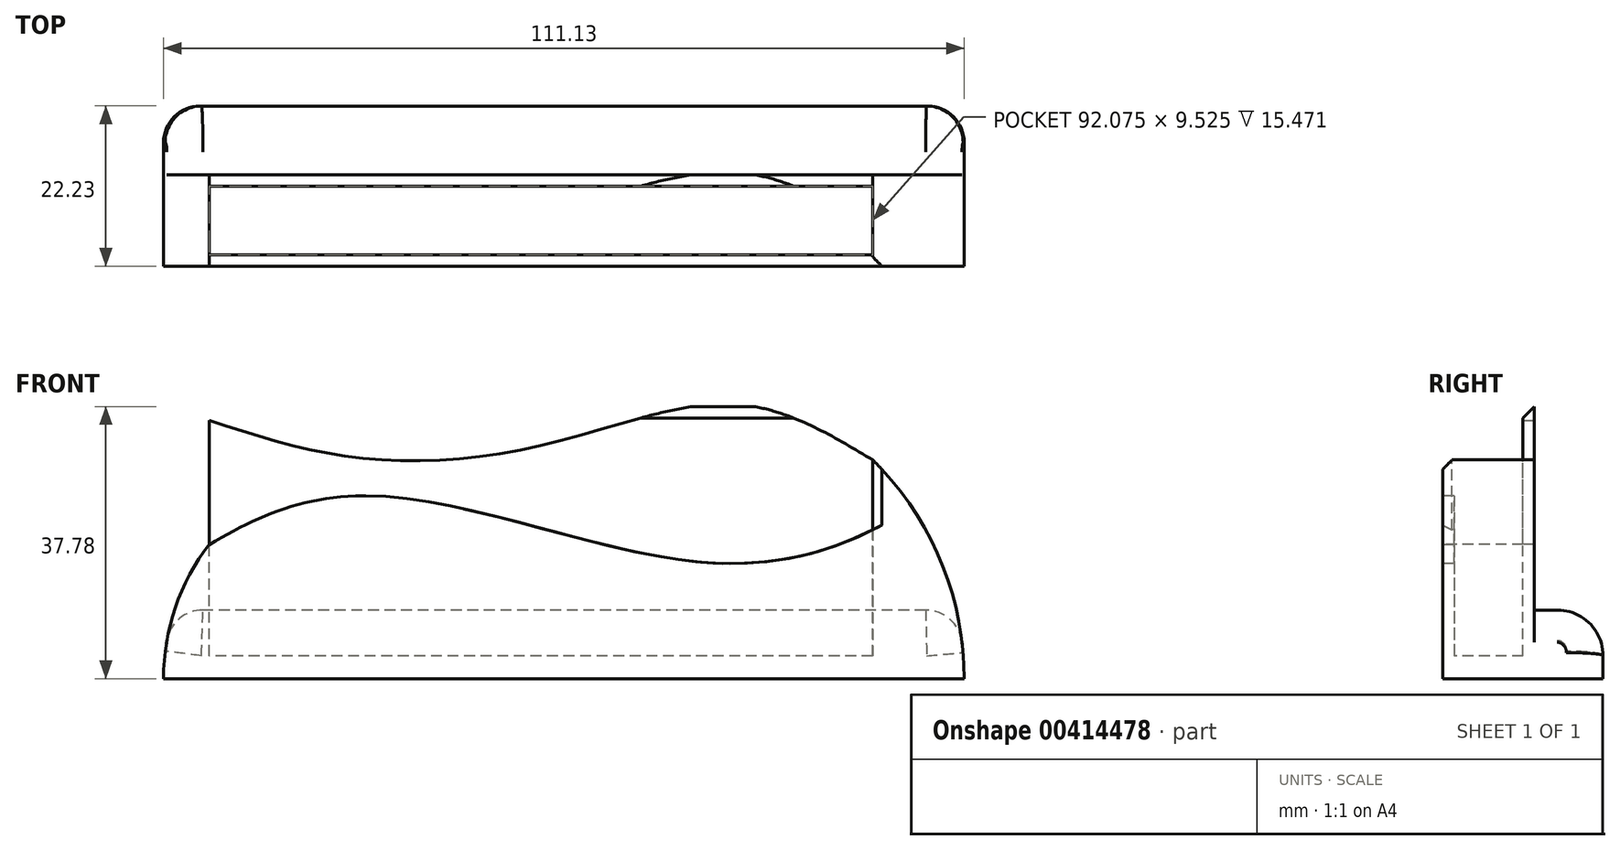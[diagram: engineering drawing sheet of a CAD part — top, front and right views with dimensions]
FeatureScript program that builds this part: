
annotation { "Feature Type Name" : "Feature", "Feature Type Description" : "" }
export const myFeature = defineFeature(function(context is Context, id is Id, definition is map)
    precondition{}
    {
        {
            var Q0;
            Q0=qCreatedBy(makeId("Right.planeOp"),FACE);
            var sketch = newSketch(context, id + "F0", { "sketchPlane" : qUnion([Q0])});
            skLineSegment(sketch, "E0", {"start": v(0, 0) * mm, "end": v(0, 25.4) * mm});
            skLineSegment(sketch, "E1", {"start": v(0, 25.4) * mm, "end": v(1.59, 25.4) * mm});
            skLineSegment(sketch, "E2", {"start": v(1.59, 25.4) * mm, "end": v(1.59, 3.18) * mm});
            skLineSegment(sketch, "E3", {"start": v(1.59, 3.18) * mm, "end": v(11.11, 3.18) * mm});
            skLineSegment(sketch, "E4", {"start": v(11.11, 3.18) * mm, "end": v(11.11, 38.1) * mm});
            skLineSegment(sketch, "E5", {"start": v(11.11, 38.1) * mm, "end": v(12.7, 38.1) * mm});
            skLineSegment(sketch, "E6", {"start": v(12.7, 38.1) * mm, "end": v(12.7, 0) * mm});
            skLineSegment(sketch, "E7", {"start": v(12.7, 0) * mm, "end": v(0, 0) * mm});
            skSolve(sketch);
        }
        {
            var Q0;
            Q0=makeQuery(id+"F0.imprint","IMPRINT",FACE,{"disambiguationData":[TD([[makeQuery(id+"F0.imprint","IMPRINT",EDGE,{"derivedFrom":sQuery(id+"F0.wireOp",EDGE,"E0")}),-1.0]])]});
            extrude(context, id + "F1", {"entities" : qUnion([Q0]), "depth" : 92.07 * mm});
        }
        {
            var Q0;
            Q0=makeQuery(id+"F1.opExtrude","SWEPT_FACE",FACE,{"disambiguationData":[OSD([sQuery(id+"F0.wireOp",EDGE,"E0")])]});
            var sketch = newSketch(context, id + "F2", { "sketchPlane" : qUnion([Q0])});
            skFitSpline(sketch, "E8", {"points": [v(0, 18.6) * mm, v(21.38, 25.4) * mm, v(56.78, 18.13) * mm, v(92.08, 20.65) * mm], "startDerivative": vector(67.88, 41.03) * mm, "endDerivative": vector(105.85, 52.89) * mm});
            skSolve(sketch);
        }
        {
            var Q0;
            {var subQ0=sQuery(id+"F0.wireOp",EDGE,"E0");var subQ1=makeQuery(id+"F1.opExtrude","CAP_EDGE",EDGE,{"disambiguationData":[OSD([subQ0])],"isStart":true});var subQ2=sQuery(id+"F2.wireOp",EDGE,"E8");var subQ3=makeQuery(id+"F2.imprint","INTERSECT",VERTEX,{"derivedFrom":[subQ1,subQ2]});Q0=makeQuery(id+"F2.imprint","IMPRINT",FACE,{"disambiguationData":[TD([[makeQuery(id+"F2.imprint","IMPRINT",EDGE,{"disambiguationData":[TD([[subQ3,-1.0]])],"derivedFrom":subQ2}),1.0]])]});}
            var Q1;
            {var subQ0=sQuery(id+"F0.wireOp",EDGE,"E0");var subQ1=makeQuery(id+"F1.opExtrude","CAP_EDGE",EDGE,{"disambiguationData":[OSD([subQ0])],"isStart":false});var subQ2=sQuery(id+"F2.wireOp",EDGE,"E8");var subQ3=makeQuery(id+"F2.imprint","INTERSECT",VERTEX,{"derivedFrom":[subQ1,subQ2]});Q1=makeQuery(id+"F2.imprint","IMPRINT",FACE,{"disambiguationData":[TD([[makeQuery(id+"F2.imprint","IMPRINT",EDGE,{"disambiguationData":[TD([[subQ3,1.0]])],"derivedFrom":subQ2}),1.0]])]});}
            extrude(context, id + "F3", {"entities" : qUnion([Q0, Q1]), "operationType" : NewBodyOperationType.REMOVE, "endBound" : BoundingType.UP_TO_NEXT, "oppositeDirection" : true, "depth" : 25.4 * mm, "offsetDistance" : 25.4 * mm});
        }
        {
            var Q0;
            Q0=makeQuery(id+"F1.opExtrude","SWEPT_FACE",FACE,{"disambiguationData":[OSD([sQuery(id+"F0.wireOp",EDGE,"E6")])]});
            var sketch = newSketch(context, id + "F4", { "sketchPlane" : qUnion([Q0])});
            skFitSpline(sketch, "E9", {"points": [v(-92.08, 30.36) * mm, v(-72.87, 38.1) * mm, v(-46.83, 32.53) * mm, v(-20.34, 30.7) * mm, v(0, 35.84) * mm], "startDerivative": vector(78.4, 47.13) * mm, "endDerivative": vector(83.06, 27.16) * mm});
            skSolve(sketch);
        }
        {
            var Q0;
            {var subQ0=sQuery(id+"F0.wireOp",EDGE,"E6");var subQ1=makeQuery(id+"F1.opExtrude","CAP_EDGE",EDGE,{"disambiguationData":[OSD([subQ0])],"isStart":false});var subQ2=sQuery(id+"F4.wireOp",EDGE,"E9");var subQ3=makeQuery(id+"F4.imprint","INTERSECT",VERTEX,{"derivedFrom":[subQ1,subQ2]});Q0=makeQuery(id+"F4.imprint","IMPRINT",FACE,{"disambiguationData":[TD([[makeQuery(id+"F4.imprint","IMPRINT",EDGE,{"disambiguationData":[TD([[subQ3,-1.0]])],"derivedFrom":subQ2}),1.0]])]});}
            var Q1;
            {var subQ0=sQuery(id+"F0.wireOp",EDGE,"E6");var subQ1=makeQuery(id+"F1.opExtrude","CAP_EDGE",EDGE,{"disambiguationData":[OSD([subQ0])],"isStart":true});var subQ2=sQuery(id+"F4.wireOp",EDGE,"E9");var subQ3=makeQuery(id+"F4.imprint","INTERSECT",VERTEX,{"derivedFrom":[subQ1,subQ2]});Q1=makeQuery(id+"F4.imprint","IMPRINT",FACE,{"disambiguationData":[TD([[makeQuery(id+"F4.imprint","IMPRINT",EDGE,{"disambiguationData":[TD([[subQ3,1.0]])],"derivedFrom":subQ2}),1.0]])]});}
            extrude(context, id + "F5", {"entities" : qUnion([Q0, Q1]), "operationType" : NewBodyOperationType.REMOVE, "endBound" : BoundingType.UP_TO_NEXT, "oppositeDirection" : true, "depth" : 25.4 * mm, "offsetDistance" : 25.4 * mm});
        }
        {
            var Q0;
            Q0=makeQuery(id+"F1.opExtrude","SWEPT_FACE",FACE,{"disambiguationData":[OSD([sQuery(id+"F0.wireOp",EDGE,"E0")])]});
            var sketch = newSketch(context, id + "F6", { "sketchPlane" : qUnion([Q0])});
            skText(sketch, "E10", { "text": "FELONY", "fontName": "Tinos-Bold.ttf"});
            skLineSegment(sketch, "E11", {"start": v(46.04, 0) * mm, "end": v(46.04, 18.7) * mm, "construction": true});
            const initialGuessF6  = {"E10": [0.00287, 0.00127, 1, 0, 0.01499]};
            skSetInitialGuess(sketch, initialGuessF6);
            skSolve(sketch);
        }
        {
            var Q0;
            Q0=makeQuery(id+"F1.opExtrude","CAP_FACE",FACE,{"disambiguationData":[OSD([sQuery(id+"F0.wireOp",EDGE,"E0"),sQuery(id+"F0.wireOp",EDGE,"E1"),sQuery(id+"F0.wireOp",EDGE,"E2"),sQuery(id+"F0.wireOp",EDGE,"E3"),sQuery(id+"F0.wireOp",EDGE,"E4"),sQuery(id+"F0.wireOp",EDGE,"E5"),sQuery(id+"F0.wireOp",EDGE,"E6"),sQuery(id+"F0.wireOp",EDGE,"E7")])],"isStart":true});
            var sketch = newSketch(context, id + "F7", { "sketchPlane" : qUnion([Q0])});
            skLineSegment(sketch, "E12", {"start": v(-12.7, 3.18) * mm, "end": v(0, 3.17) * mm});
            skSolve(sketch);
        }
        {
            var Q0;
            {var subQ3=makeQuery(id+"F1.opExtrude","CAP_EDGE",EDGE,{"disambiguationData":[OSD([sQuery(id+"F0.wireOp",EDGE,"E7")])],"isStart":true});Q0=makeQuery(id+"F7.imprint","IMPRINT",FACE,{"disambiguationData":[TD([[makeQuery(id+"F7.imprint","IMPRINT",EDGE,{"derivedFrom":subQ3}),1.0]])]});}
            extrude(context, id + "F8", {"entities" : qUnion([Q0]), "operationType" : NewBodyOperationType.ADD, "depth" : 6.35 * mm});
        }
        {
            var Q0;
            Q0=makeQuery(id+"F8.boolean.opBoolean","MERGE",FACE,{"derivedFrom":[makeQuery(id+"F1.opExtrude","SWEPT_FACE",FACE,{"disambiguationData":[OSD([sQuery(id+"F0.wireOp",EDGE,"E3")])]}),makeQuery(id+"F8.opExtrude","SWEPT_FACE",FACE,{"disambiguationData":[OSD([sQuery(id+"F7.wireOp",EDGE,"E12")])]})]});
            var sketch = newSketch(context, id + "F9", { "sketchPlane" : qUnion([Q0])});
            skLineSegment(sketch, "E13", {"start": v(0, 11.11) * mm, "end": v(0, 1.59) * mm});
            skSolve(sketch);
        }
        {
            var Q0;
            Q0=makeQuery(id+"F9.imprint","IMPRINT",FACE,{"disambiguationData":[TD([[makeQuery(id+"F9.imprint","IMPRINT",EDGE,{"derivedFrom":sQuery(id+"F9.wireOp",EDGE,"E13")}),-1.0]])]});
            extrude(context, id + "F10", {"entities" : qUnion([Q0]), "operationType" : NewBodyOperationType.ADD, "depth" : 15.47 * mm});
        }
        {
            var Q0;
            {var subQ0=sQuery(id+"F0.wireOp",EDGE,"E0");var subQ1=sQuery(id+"F0.wireOp",EDGE,"E1");Q0=makeQuery(id+"F10.boolean.opBoolean","MERGE",FACE,{"derivedFrom":[makeQuery(id+"F8.boolean.opBoolean","MERGE",FACE,{"derivedFrom":[makeQuery(id+"FmbjE0y4cJYNi4l_1.boolean.opBoolean","SPLIT",FACE,{"disambiguationData":[TD([makeQuery(id+"F1.opExtrude","SWEPT_FACE",FACE,{"disambiguationData":[OSD([subQ1])]})])],"derivedFrom":makeQuery(id+"F1.opExtrude","SWEPT_FACE",FACE,{"disambiguationData":[OSD([subQ0])]})}),makeQuery(id+"F8.opExtrude","SWEPT_FACE",FACE,{"disambiguationData":[OSD([subQ0])]})]}),makeQuery(id+"F10.opExtrude","SWEPT_FACE",FACE,{"disambiguationData":[OSD([subQ0,sQuery(id+"F7.wireOp",EDGE,"E12")])]})]});}
            var sketch = newSketch(context, id + "F11", { "sketchPlane" : qUnion([Q0])});
            skArc(sketch, "E14", {"start": v(0, 18.65) * mm, "mid": v(-4.72, 9.85) * mm, "end": v(-6.35, 0) * mm});
            skSolve(sketch);
        }
        {
            var Q0;
            Q0=makeQuery(id+"F11.imprint","IMPRINT",FACE,{"disambiguationData":[TD([[makeQuery(id+"F11.imprint","IMPRINT",EDGE,{"derivedFrom":sQuery(id+"F11.wireOp",EDGE,"E14")}),-1.0]])]});
            extrude(context, id + "F12", {"entities" : qUnion([Q0]), "operationType" : NewBodyOperationType.REMOVE, "endBound" : BoundingType.UP_TO_NEXT, "oppositeDirection" : true, "depth" : 25.4 * mm});
        }
        {
            var Q0;
            Q0=makeQuery(id+"F1.opExtrude","CAP_FACE",FACE,{"disambiguationData":[OSD([sQuery(id+"F0.wireOp",EDGE,"E0"),sQuery(id+"F0.wireOp",EDGE,"E1"),sQuery(id+"F0.wireOp",EDGE,"E2"),sQuery(id+"F0.wireOp",EDGE,"E3"),sQuery(id+"F0.wireOp",EDGE,"E4"),sQuery(id+"F0.wireOp",EDGE,"E5"),sQuery(id+"F0.wireOp",EDGE,"E6"),sQuery(id+"F0.wireOp",EDGE,"E7")])],"isStart":false});
            var sketch = newSketch(context, id + "F13", { "sketchPlane" : qUnion([Q0])});
            skLineSegment(sketch, "E15", {"start": v(0, 20.65) * mm, "end": v(0, 30.36) * mm});
            skLineSegment(sketch, "E16", {"start": v(0, 30.36) * mm, "end": v(12.7, 30.36) * mm});
            skSolve(sketch);
        }
        {
            var Q0;
            Q0=makeQuery(id+"F13.imprint","IMPRINT",FACE,{"disambiguationData":[TD([[makeQuery(id+"F13.imprint","IMPRINT",EDGE,{"derivedFrom":makeQuery(id+"F1.opExtrude","CAP_EDGE",EDGE,{"disambiguationData":[OSD([sQuery(id+"F0.wireOp",EDGE,"E3")])],"isStart":false})}),-1.0]])]});
            var Q1;
            {var subQ4=sQuery(id+"F13.wireOp",EDGE,"E15");Q1=makeQuery(id+"F13.imprint","IMPRINT",FACE,{"disambiguationData":[TD([[makeQuery(id+"F13.imprint","IMPRINT",EDGE,{"derivedFrom":subQ4}),-1.0]])]});}
            extrude(context, id + "F14", {"entities" : qUnion([Q0, Q1]), "operationType" : NewBodyOperationType.ADD, "depth" : 12.7 * mm});
        }
        {
            var Q0;
            {var subQ0=sQuery(id+"F0.wireOp",EDGE,"E6");Q0=makeQuery(id+"F14.boolean.opBoolean","MERGE",FACE,{"derivedFrom":[makeQuery(id+"F10.boolean.opBoolean","MERGE",FACE,{"derivedFrom":[makeQuery(id+"F8.boolean.opBoolean","MERGE",FACE,{"derivedFrom":[makeQuery(id+"F1.opExtrude","SWEPT_FACE",FACE,{"disambiguationData":[OSD([subQ0])]}),makeQuery(id+"F8.opExtrude","SWEPT_FACE",FACE,{"disambiguationData":[OSD([subQ0])]})]}),makeQuery(id+"F10.opExtrude","SWEPT_FACE",FACE,{"disambiguationData":[OSD([subQ0,sQuery(id+"F7.wireOp",EDGE,"E12")])]})]}),makeQuery(id+"F14.opExtrude","SWEPT_FACE",FACE,{"disambiguationData":[OSD([subQ0])]})]});}
            var sketch = newSketch(context, id + "F15", { "sketchPlane" : qUnion([Q0])});
            skArc(sketch, "E17", {"start": v(-92.08, 30.36) * mm, "mid": v(-101.47, 16.46) * mm, "end": v(-104.78, 0) * mm});
            skSolve(sketch);
        }
        {
            var Q0;
            Q0=makeQuery(id+"F15.imprint","IMPRINT",FACE,{"disambiguationData":[TD([[makeQuery(id+"F15.imprint","IMPRINT",EDGE,{"derivedFrom":sQuery(id+"F15.wireOp",EDGE,"E17")}),-1.0]])]});
            extrude(context, id + "F16", {"entities" : qUnion([Q0]), "operationType" : NewBodyOperationType.REMOVE, "endBound" : BoundingType.UP_TO_NEXT, "oppositeDirection" : true, "depth" : 25.4 * mm});
        }
        {
            var Q0;
            {var subQ0=sQuery(id+"F0.wireOp",EDGE,"E6");Q0=makeQuery(id+"F14.boolean.opBoolean","MERGE",FACE,{"derivedFrom":[makeQuery(id+"F10.boolean.opBoolean","MERGE",FACE,{"derivedFrom":[makeQuery(id+"F8.boolean.opBoolean","MERGE",FACE,{"derivedFrom":[makeQuery(id+"F1.opExtrude","SWEPT_FACE",FACE,{"disambiguationData":[OSD([subQ0])]}),makeQuery(id+"F8.opExtrude","SWEPT_FACE",FACE,{"disambiguationData":[OSD([subQ0])]})]}),makeQuery(id+"F10.opExtrude","SWEPT_FACE",FACE,{"disambiguationData":[OSD([subQ0,sQuery(id+"F7.wireOp",EDGE,"E12")])]})]}),makeQuery(id+"F14.opExtrude","SWEPT_FACE",FACE,{"disambiguationData":[OSD([subQ0])]})]});}
            var sketch = newSketch(context, id + "F17", { "sketchPlane" : qUnion([Q0])});
            skLineSegment(sketch, "E18", {"start": v(-103.7, 9.53) * mm, "end": v(4.83, 9.53) * mm});
            skSolve(sketch);
        }
        {
            var Q0;
            {var subQ1=sQuery(id+"F17.wireOp",EDGE,"E18");Q0=makeQuery(id+"F17.imprint","IMPRINT",FACE,{"disambiguationData":[TD([[makeQuery(id+"F17.imprint","IMPRINT",EDGE,{"derivedFrom":subQ1}),-1.0]])]});}
            extrude(context, id + "F18", {"entities" : qUnion([Q0]), "operationType" : NewBodyOperationType.ADD, "depth" : 9.52 * mm});
        }
        {
            var Q0;
            Q0=makeQuery(id+"F18.opExtrude","CAP_EDGE",EDGE,{"disambiguationData":[OSD([sQuery(id+"F17.wireOp",EDGE,"E18")])],"isStart":false});
            fillet(context, id + "F19", {"entities" : qUnion([Q0]), "radius" : 6.35 * mm, "tangentPropagation" : true, "allowEdgeOverflow" : false});
        }
        {
            var Q0;
            {var subQ0=sQuery(id+"F15.wireOp",EDGE,"E17");Q0=makeQuery(id+"F19.opFillet","BLEND_EDGE",EDGE,{"blendedFrom":[makeQuery(id+"F18.opExtrude","CAP_EDGE",EDGE,{"disambiguationData":[OSD([sQuery(id+"F17.wireOp",EDGE,"E18")])],"isStart":false}),makeQuery(id+"F18.boolean.opBoolean","MERGE",FACE,{"derivedFrom":[makeQuery(id+"F16.boolean.opBoolean","COPY",FACE,{"derivedFrom":makeQuery(id+"F16.opExtrude","SWEPT_FACE",FACE,{"disambiguationData":[OSD([subQ0])]})}),makeQuery(id+"F18.opExtrude","SWEPT_FACE",FACE,{"disambiguationData":[OSD([subQ0])]})]})],"blendedInto":[makeQuery(id+"F18.boolean.opBoolean","MERGE",FACE,{"derivedFrom":[makeQuery(id+"F16.boolean.opBoolean","COPY",FACE,{"derivedFrom":makeQuery(id+"F16.opExtrude","SWEPT_FACE",FACE,{"disambiguationData":[OSD([subQ0])]})}),makeQuery(id+"F18.opExtrude","SWEPT_FACE",FACE,{"disambiguationData":[OSD([subQ0])]})]})]});}
            var Q1;
            {var subQ0=sQuery(id+"F11.wireOp",EDGE,"E14");Q1=makeQuery(id+"F19.opFillet","BLEND_EDGE",EDGE,{"blendedFrom":[makeQuery(id+"F18.opExtrude","CAP_EDGE",EDGE,{"disambiguationData":[OSD([sQuery(id+"F17.wireOp",EDGE,"E18")])],"isStart":false}),makeQuery(id+"F18.boolean.opBoolean","MERGE",FACE,{"derivedFrom":[makeQuery(id+"F12.boolean.opBoolean","COPY",FACE,{"derivedFrom":makeQuery(id+"F12.opExtrude","SWEPT_FACE",FACE,{"disambiguationData":[OSD([subQ0])]})}),makeQuery(id+"F18.opExtrude","SWEPT_FACE",FACE,{"disambiguationData":[OSD([sQuery(id+"F0.wireOp",EDGE,"E6"),sQuery(id+"F7.wireOp",EDGE,"E12"),subQ0])]})]})],"blendedInto":[makeQuery(id+"F18.boolean.opBoolean","MERGE",FACE,{"derivedFrom":[makeQuery(id+"F12.boolean.opBoolean","COPY",FACE,{"derivedFrom":makeQuery(id+"F12.opExtrude","SWEPT_FACE",FACE,{"disambiguationData":[OSD([subQ0])]})}),makeQuery(id+"F18.opExtrude","SWEPT_FACE",FACE,{"disambiguationData":[OSD([sQuery(id+"F0.wireOp",EDGE,"E6"),sQuery(id+"F7.wireOp",EDGE,"E12"),subQ0])]})]})]});}
            fillet(context, id + "F20", {"entities" : qUnion([Q0, Q1]), "radius" : 5.08 * mm, "tangentPropagation" : true, "allowEdgeOverflow" : false});
        }
        {
            var Q0;
            {var subQ0=sQuery(id+"F0.wireOp",EDGE,"E0");var subQ2=sQuery(id+"F0.wireOp",EDGE,"E1");Q0=makeQuery(id+"F16.boolean.opBoolean","COPY",EDGE,{"derivedFrom":makeQuery(id+"F16.opExtrude","TWEAK_EDGE",EDGE,{"derivedFrom":[makeQuery(id+"F14.boolean.opBoolean","MERGE",FACE,{"derivedFrom":[makeQuery(id+"F10.boolean.opBoolean","MERGE",FACE,{"derivedFrom":[makeQuery(id+"F8.boolean.opBoolean","MERGE",FACE,{"derivedFrom":[makeQuery(id+"FmbjE0y4cJYNi4l_1.boolean.opBoolean","SPLIT",FACE,{"disambiguationData":[TD([makeQuery(id+"F1.opExtrude","SWEPT_FACE",FACE,{"disambiguationData":[OSD([subQ2])]})])],"derivedFrom":makeQuery(id+"F1.opExtrude","SWEPT_FACE",FACE,{"disambiguationData":[OSD([subQ0])]})}),makeQuery(id+"F8.opExtrude","SWEPT_FACE",FACE,{"disambiguationData":[OSD([subQ0])]})]}),makeQuery(id+"F10.opExtrude","SWEPT_FACE",FACE,{"disambiguationData":[OSD([subQ0,sQuery(id+"F7.wireOp",EDGE,"E12")])]})]}),makeQuery(id+"F14.opExtrude","SWEPT_FACE",FACE,{"disambiguationData":[OSD([subQ0,sQuery(id+"F13.wireOp",EDGE,"E15")])]})]}),makeQuery(id+"F15.imprint","IMPRINT",EDGE,{"derivedFrom":sQuery(id+"F15.wireOp",EDGE,"E17")})]})});}
            var Q1;
            Q1=makeQuery(id+"F14.opExtrude","CAP_EDGE",EDGE,{"disambiguationData":[OSD([sQuery(id+"F0.wireOp",EDGE,"E0"),sQuery(id+"F13.wireOp",EDGE,"E15")])],"isStart":true});
            var Q2;
            {var subQ0=sQuery(id+"F2.wireOp",EDGE,"E8");var subQ1=sQuery(id+"F0.wireOp",EDGE,"E0");Q2=makeQuery(id+"F3.boolean.opBoolean","COPY",EDGE,{"derivedFrom":makeQuery(id+"F3.opExtrude","CAP_EDGE",EDGE,{"disambiguationData":[OSD([subQ0]),TDD([makeQuery(id+"F2.imprint","IMPRINT",EDGE,{"disambiguationData":[TD([[makeQuery(id+"F2.imprint","INTERSECT",VERTEX,{"derivedFrom":[makeQuery(id+"F1.opExtrude","CAP_EDGE",EDGE,{"disambiguationData":[OSD([subQ1])],"isStart":false}),subQ0]}),1.0]])],"derivedFrom":subQ0})])],"isStart":true})});}
            var Q3;
            Q3=makeQuery(id+"F12.boolean.opBoolean","COPY",EDGE,{"derivedFrom":makeQuery(id+"F12.opExtrude","CAP_EDGE",EDGE,{"disambiguationData":[OSD([sQuery(id+"F11.wireOp",EDGE,"E14")])],"isStart":true})});
            var Q4;
            {var subQ0=sQuery(id+"F2.wireOp",EDGE,"E8");var subQ1=sQuery(id+"F0.wireOp",EDGE,"E0");Q4=makeQuery(id+"F3.boolean.opBoolean","COPY",EDGE,{"derivedFrom":makeQuery(id+"F3.opExtrude","CAP_EDGE",EDGE,{"disambiguationData":[OSD([subQ0]),TDD([makeQuery(id+"F2.imprint","IMPRINT",EDGE,{"disambiguationData":[TD([[makeQuery(id+"F2.imprint","INTERSECT",VERTEX,{"derivedFrom":[makeQuery(id+"F1.opExtrude","CAP_EDGE",EDGE,{"disambiguationData":[OSD([subQ1])],"isStart":true}),subQ0]}),-1.0]])],"derivedFrom":subQ0})])],"isStart":true})});}
            chamfer(context, id + "F21", {"entities" : qUnion([Q0, Q1, Q2, Q3, Q4]), "width" : 1.27 * mm, "tangentPropagation" : true});
        }
        {
            var Q0;
            {var subQ0=sQuery(id+"F4.wireOp",EDGE,"E9");var subQ1=sQuery(id+"F0.wireOp",EDGE,"E6");Q0=makeQuery(id+"F5.boolean.opBoolean","COPY",EDGE,{"derivedFrom":makeQuery(id+"F5.opExtrude","TWEAK_EDGE",EDGE,{"derivedFrom":[makeQuery(id+"F1.opExtrude","SWEPT_FACE",FACE,{"disambiguationData":[OSD([sQuery(id+"F0.wireOp",EDGE,"E4")])]}),makeQuery(id+"F4.imprint","IMPRINT",EDGE,{"disambiguationData":[TD([[makeQuery(id+"F4.imprint","INTERSECT",VERTEX,{"derivedFrom":[makeQuery(id+"F1.opExtrude","CAP_EDGE",EDGE,{"disambiguationData":[OSD([subQ1])],"isStart":true}),subQ0]}),1.0]])],"derivedFrom":subQ0})]})});}
            var Q1;
            Q1=makeQuery(id+"F1.opExtrude","SWEPT_EDGE",EDGE,{"disambiguationData":[OSD([sQuery(id+"F0.wireOp",EDGE,"E4"),sQuery(id+"F0.wireOp",EDGE,"E5")])]});
            chamfer(context, id + "F22", {"entities" : qUnion([Q0, Q1]), "width" : 1.9 * mm, "tangentPropagation" : true});
        }
    });
